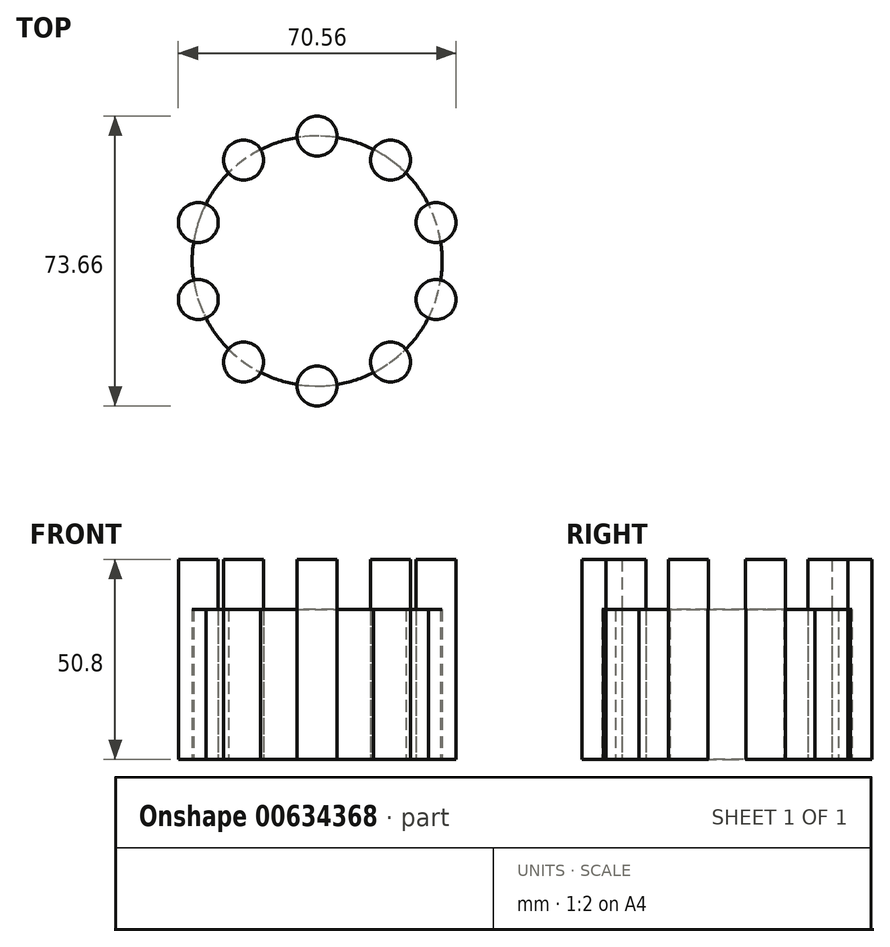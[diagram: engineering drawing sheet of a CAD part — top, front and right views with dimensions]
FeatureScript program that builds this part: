
annotation { "Feature Type Name" : "Feature", "Feature Type Description" : "" }
export const myFeature = defineFeature(function(context is Context, id is Id, definition is map)
    precondition{}
    {
        {
            var Q0;
            Q0=qCreatedBy(makeId("Top.planeOp"),FACE);
            var sketch = newSketch(context, id + "F0", { "sketchPlane" : qUnion([Q0])});
            skCircle(sketch, "E0", {"center": v(0, 0) * mm, "radius": 31.75 * mm});
            skSolve(sketch);
        }
        {
            var Q0;
            Q0=qSketchRegion(id+"F0",true);
            extrude(context, id + "F1", {"entities" : qUnion([Q0]), "depth" : 38.1 * mm});
        }
        {
            var Q0;
            Q0=qCreatedBy(makeId("Top.planeOp"),FACE);
            var sketch = newSketch(context, id + "F2", { "sketchPlane" : qUnion([Q0])});
            skCircle(sketch, "E1", {"center": v(0, 31.75) * mm, "radius": 5.08 * mm});
            skCircle(sketch, "E2.1.0", {"center": v(-18.66, 25.69) * mm, "radius": 5.08 * mm});
            skCircle(sketch, "E2.2.0", {"center": v(-30.2, 9.81) * mm, "radius": 5.08 * mm});
            skCircle(sketch, "E2.3.0", {"center": v(-30.2, -9.81) * mm, "radius": 5.08 * mm});
            skCircle(sketch, "E2.4.0", {"center": v(-18.66, -25.69) * mm, "radius": 5.08 * mm});
            skCircle(sketch, "E2.5.0", {"center": v(0, -31.75) * mm, "radius": 5.08 * mm});
            skCircle(sketch, "E2.6.0", {"center": v(18.66, -25.69) * mm, "radius": 5.08 * mm});
            skCircle(sketch, "E2.7.0", {"center": v(30.2, -9.81) * mm, "radius": 5.08 * mm});
            skCircle(sketch, "E2.8.0", {"center": v(30.2, 9.81) * mm, "radius": 5.08 * mm});
            skCircle(sketch, "E2.9.0", {"center": v(18.66, 25.69) * mm, "radius": 5.08 * mm});
            skPoint(sketch, "E2.center", {"position": v(0, 0) * mm});
            skSolve(sketch);
        }
        {
            var Q0;
            Q0=qSketchRegion(id+"F2",true);
            extrude(context, id + "F3", {"entities" : qUnion([Q0]), "depth" : 50.8 * mm});
        }
        {
            var Q0;
            Q0=makeQuery(id+"F1.opExtrude","SWEPT_BODY",BODY,{"disambiguationData":[OSD([sQuery(id+"F0.wireOp",EDGE,"E0")])]});
            var Q1;
            Q1=makeQuery(id+"F3.opExtrude","SWEPT_BODY",BODY,{"disambiguationData":[OSD([sQuery(id+"F2.wireOp",EDGE,"E1")])]});
            var Q2;
            Q2=makeQuery(id+"F3.opExtrude","SWEPT_BODY",BODY,{"disambiguationData":[OSD([sQuery(id+"F2.wireOp",EDGE,"E2.1.0")])]});
            var Q3;
            Q3=makeQuery(id+"F3.opExtrude","SWEPT_BODY",BODY,{"disambiguationData":[OSD([sQuery(id+"F2.wireOp",EDGE,"E2.2.0")])]});
            var Q4;
            Q4=makeQuery(id+"F3.opExtrude","SWEPT_BODY",BODY,{"disambiguationData":[OSD([sQuery(id+"F2.wireOp",EDGE,"E2.3.0")])]});
            var Q5;
            Q5=makeQuery(id+"F3.opExtrude","SWEPT_BODY",BODY,{"disambiguationData":[OSD([sQuery(id+"F2.wireOp",EDGE,"E2.4.0")])]});
            var Q6;
            Q6=makeQuery(id+"F3.opExtrude","SWEPT_BODY",BODY,{"disambiguationData":[OSD([sQuery(id+"F2.wireOp",EDGE,"E2.5.0")])]});
            var Q7;
            Q7=makeQuery(id+"F3.opExtrude","SWEPT_BODY",BODY,{"disambiguationData":[OSD([sQuery(id+"F2.wireOp",EDGE,"E2.6.0")])]});
            var Q8;
            Q8=makeQuery(id+"F3.opExtrude","SWEPT_BODY",BODY,{"disambiguationData":[OSD([sQuery(id+"F2.wireOp",EDGE,"E2.7.0")])]});
            var Q9;
            Q9=makeQuery(id+"F3.opExtrude","SWEPT_BODY",BODY,{"disambiguationData":[OSD([sQuery(id+"F2.wireOp",EDGE,"E2.8.0")])]});
            var Q10;
            Q10=makeQuery(id+"F3.opExtrude","SWEPT_BODY",BODY,{"disambiguationData":[OSD([sQuery(id+"F2.wireOp",EDGE,"E2.9.0")])]});
            booleanBodies(context, id + "F4", {"operationType" : BooleanOperationType.INTERSECTION, "tools" : qUnion([Q0, Q1, Q2, Q3, Q4, Q5, Q6, Q7, Q8, Q9, Q10]), "keepTools" : true});
        }
        {
            var Q0;
            Q0=makeQuery(id+"F3.opExtrude","SWEPT_BODY",BODY,{"disambiguationData":[OSD([sQuery(id+"F2.wireOp",EDGE,"E2.6.0")])]});
            var Q1;
            Q1=makeQuery(id+"F1.opExtrude","SWEPT_BODY",BODY,{"disambiguationData":[OSD([sQuery(id+"F0.wireOp",EDGE,"E0")])]});
            booleanBodies(context, id + "F5", {"operationType" : BooleanOperationType.INTERSECTION, "tools" : qUnion([Q0, Q1]), "keepTools" : true});
        }
        {
            var Q0;
            Q0=makeQuery(id+"F3.opExtrude","SWEPT_BODY",BODY,{"disambiguationData":[OSD([sQuery(id+"F2.wireOp",EDGE,"E2.5.0")])]});
            var Q1;
            Q1=makeQuery(id+"F1.opExtrude","SWEPT_BODY",BODY,{"disambiguationData":[OSD([sQuery(id+"F0.wireOp",EDGE,"E0")])]});
            booleanBodies(context, id + "F6", {"operationType" : BooleanOperationType.INTERSECTION, "tools" : qUnion([Q0, Q1]), "keepTools" : true});
        }
        {
            var Q0;
            Q0=makeQuery(id+"F3.opExtrude","SWEPT_BODY",BODY,{"disambiguationData":[OSD([sQuery(id+"F2.wireOp",EDGE,"E2.4.0")])]});
            var Q1;
            Q1=makeQuery(id+"F1.opExtrude","SWEPT_BODY",BODY,{"disambiguationData":[OSD([sQuery(id+"F0.wireOp",EDGE,"E0")])]});
            booleanBodies(context, id + "F7", {"operationType" : BooleanOperationType.INTERSECTION, "tools" : qUnion([Q0, Q1]), "keepTools" : true});
        }
        {
            var Q0;
            Q0=makeQuery(id+"F3.opExtrude","SWEPT_BODY",BODY,{"disambiguationData":[OSD([sQuery(id+"F2.wireOp",EDGE,"E2.3.0")])]});
            var Q1;
            Q1=makeQuery(id+"F1.opExtrude","SWEPT_BODY",BODY,{"disambiguationData":[OSD([sQuery(id+"F0.wireOp",EDGE,"E0")])]});
            booleanBodies(context, id + "F8", {"operationType" : BooleanOperationType.INTERSECTION, "tools" : qUnion([Q0, Q1]), "keepTools" : true});
        }
        {
            var Q0;
            Q0=makeQuery(id+"F3.opExtrude","SWEPT_BODY",BODY,{"disambiguationData":[OSD([sQuery(id+"F2.wireOp",EDGE,"E2.2.0")])]});
            var Q1;
            Q1=makeQuery(id+"F1.opExtrude","SWEPT_BODY",BODY,{"disambiguationData":[OSD([sQuery(id+"F0.wireOp",EDGE,"E0")])]});
            booleanBodies(context, id + "F9", {"operationType" : BooleanOperationType.INTERSECTION, "tools" : qUnion([Q0, Q1]), "keepTools" : true});
        }
        {
            var Q0;
            Q0=makeQuery(id+"F3.opExtrude","SWEPT_BODY",BODY,{"disambiguationData":[OSD([sQuery(id+"F2.wireOp",EDGE,"E2.1.0")])]});
            var Q1;
            Q1=makeQuery(id+"F1.opExtrude","SWEPT_BODY",BODY,{"disambiguationData":[OSD([sQuery(id+"F0.wireOp",EDGE,"E0")])]});
            booleanBodies(context, id + "F10", {"operationType" : BooleanOperationType.INTERSECTION, "tools" : qUnion([Q0, Q1]), "keepTools" : true});
        }
        {
            var Q0;
            Q0=makeQuery(id+"F3.opExtrude","SWEPT_BODY",BODY,{"disambiguationData":[OSD([sQuery(id+"F2.wireOp",EDGE,"E1")])]});
            var Q1;
            Q1=makeQuery(id+"F1.opExtrude","SWEPT_BODY",BODY,{"disambiguationData":[OSD([sQuery(id+"F0.wireOp",EDGE,"E0")])]});
            booleanBodies(context, id + "F11", {"operationType" : BooleanOperationType.INTERSECTION, "tools" : qUnion([Q0, Q1]), "keepTools" : true});
        }
        {
            var Q0;
            Q0=makeQuery(id+"F3.opExtrude","SWEPT_BODY",BODY,{"disambiguationData":[OSD([sQuery(id+"F2.wireOp",EDGE,"E2.9.0")])]});
            var Q1;
            Q1=makeQuery(id+"F1.opExtrude","SWEPT_BODY",BODY,{"disambiguationData":[OSD([sQuery(id+"F0.wireOp",EDGE,"E0")])]});
            booleanBodies(context, id + "F12", {"operationType" : BooleanOperationType.INTERSECTION, "tools" : qUnion([Q0, Q1]), "keepTools" : true});
        }
        {
            var Q0;
            Q0=makeQuery(id+"F3.opExtrude","SWEPT_BODY",BODY,{"disambiguationData":[OSD([sQuery(id+"F2.wireOp",EDGE,"E2.8.0")])]});
            var Q1;
            Q1=makeQuery(id+"F1.opExtrude","SWEPT_BODY",BODY,{"disambiguationData":[OSD([sQuery(id+"F0.wireOp",EDGE,"E0")])]});
            booleanBodies(context, id + "F13", {"operationType" : BooleanOperationType.INTERSECTION, "tools" : qUnion([Q0, Q1]), "keepTools" : true});
        }
        {
            var Q0;
            Q0=makeQuery(id+"F3.opExtrude","SWEPT_BODY",BODY,{"disambiguationData":[OSD([sQuery(id+"F2.wireOp",EDGE,"E2.7.0")])]});
            var Q1;
            Q1=makeQuery(id+"F1.opExtrude","SWEPT_BODY",BODY,{"disambiguationData":[OSD([sQuery(id+"F0.wireOp",EDGE,"E0")])]});
            booleanBodies(context, id + "F14", {"operationType" : BooleanOperationType.INTERSECTION, "tools" : qUnion([Q0, Q1]), "keepTools" : true});
        }
    });
